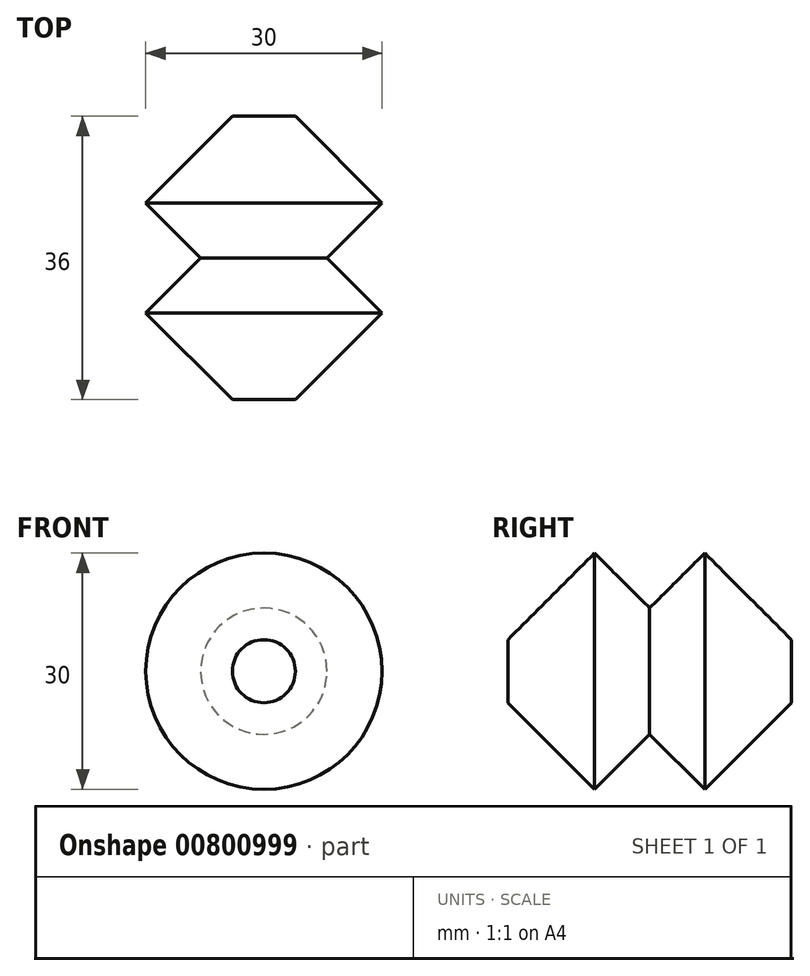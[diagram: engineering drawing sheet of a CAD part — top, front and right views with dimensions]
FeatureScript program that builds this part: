
annotation { "Feature Type Name" : "Feature", "Feature Type Description" : "" }
export const myFeature = defineFeature(function(context is Context, id is Id, definition is map)
    precondition{}
    {
        {
            var Q0;
            Q0=qCreatedBy(makeId("Top.planeOp"),FACE);
            var sketch = newSketch(context, id + "F0", { "sketchPlane" : qUnion([Q0])});
            skLineSegment(sketch, "E0", {"start": v(0, 0) * mm, "end": v(0, -36) * mm});
            skLineSegment(sketch, "E1", {"start": v(0, -36) * mm, "end": v(4, -36) * mm});
            skLineSegment(sketch, "E2", {"start": v(0, 0) * mm, "end": v(4, 0) * mm});
            skLineSegment(sketch, "E3", {"start": v(4, -4) * mm, "end": v(4, -32) * mm});
            skLineSegment(sketch, "E4", {"start": v(4, 0) * mm, "end": v(15, -11) * mm});
            skLineSegment(sketch, "E5", {"start": v(15, -25) * mm, "end": v(4, -36) * mm});
            skLineSegment(sketch, "E6", {"start": v(4, -4) * mm, "end": v(11, -11) * mm});
            skLineSegment(sketch, "E7", {"start": v(15, -11) * mm, "end": v(8.02, -18) * mm});
            skLineSegment(sketch, "E8", {"start": v(8.02, -18) * mm, "end": v(15, -25) * mm});
            skLineSegment(sketch, "E9", {"start": v(4, -32) * mm, "end": v(11, -25) * mm});
            skLineSegment(sketch, "E10", {"start": v(11, -11) * mm, "end": v(15, -11) * mm, "construction": true});
            skLineSegment(sketch, "E11", {"start": v(11, -25) * mm, "end": v(4, -18.1) * mm});
            skLineSegment(sketch, "E12", {"start": v(4, -18.1) * mm, "end": v(4, -17.9) * mm});
            skLineSegment(sketch, "E13", {"start": v(4, -17.9) * mm, "end": v(11, -11) * mm});
            skLineSegment(sketch, "E14", {"start": v(8.02, -18) * mm, "end": v(4, -18) * mm, "construction": true});
            skSolve(sketch);
        }
        {
            var Q0;
            {var subQ0=sQuery(id+"F0.wireOp",EDGE,"E6");Q0=makeQuery(id+"F0.imprint","IMPRINT",FACE,{"disambiguationData":[TD([[makeQuery(id+"F0.imprint","IMPRINT",EDGE,{"derivedFrom":subQ0}),-1.0]])]});}
            var Q1;
            Q1=makeQuery(id+"F0.imprint","IMPRINT",FACE,{"disambiguationData":[TD([[makeQuery(id+"F0.imprint","IMPRINT",EDGE,{"derivedFrom":sQuery(id+"F0.wireOp",EDGE,"E0")}),1.0]])]});
            var Q2;
            {var subQ0=sQuery(id+"F0.wireOp",EDGE,"E9");Q2=makeQuery(id+"F0.imprint","IMPRINT",FACE,{"disambiguationData":[TD([[makeQuery(id+"F0.imprint","IMPRINT",EDGE,{"derivedFrom":subQ0}),1.0]])]});}
            var Q3;
            Q3=sQuery(id+"F0.wireOp",EDGE,"E0");
            revolve(context, id + "F1", {"surfaceOperationType" : NewSurfaceOperationType.NEW, "entities" : qUnion([Q0, Q1, Q2]), "axis" : qUnion([Q3]), "revolveType" : RevolveType.FULL});
        }
    });
